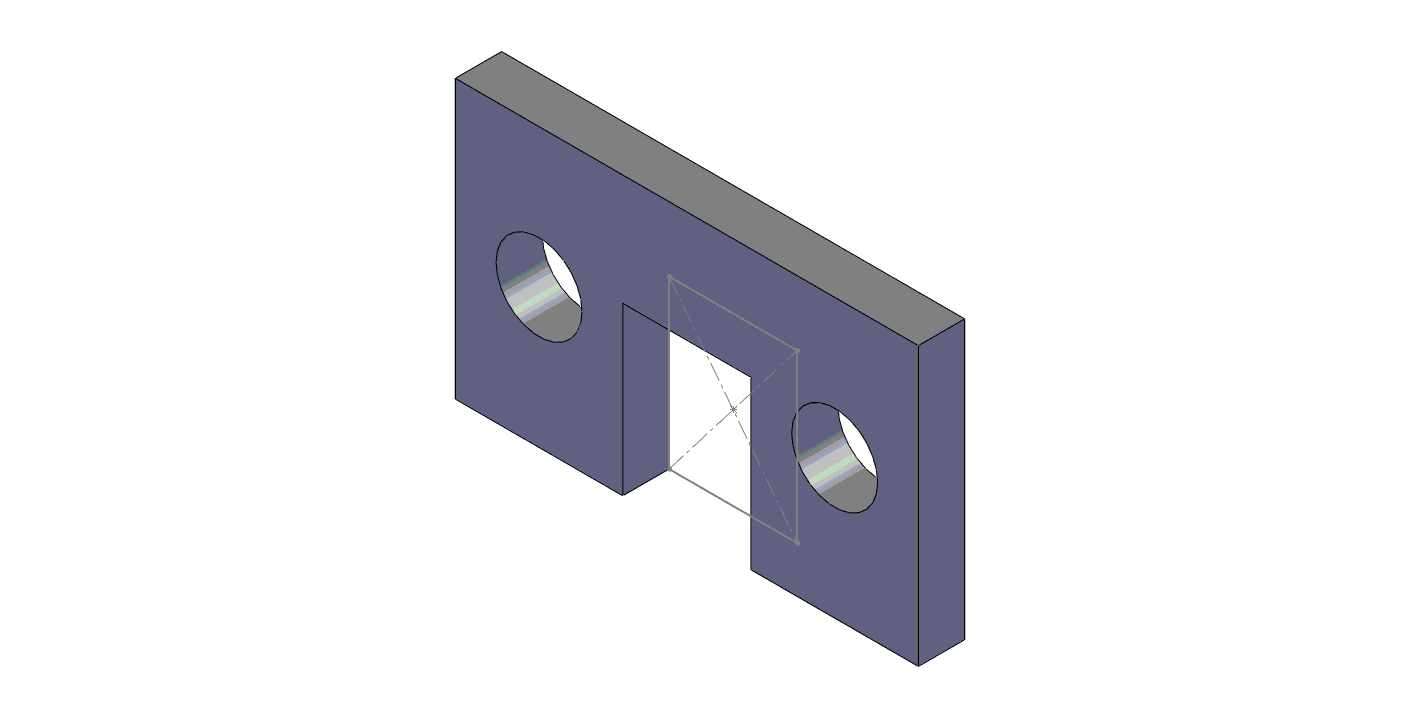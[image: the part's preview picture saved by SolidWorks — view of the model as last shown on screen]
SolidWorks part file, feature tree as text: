
SOLIDWORKS PART (.sldprt)
format: sldprt  version: not decoded by parser v0  size: 173,056 bytes
history: native  units: mm
features: sketch x4, material x1, extrude x1, hole x1 (+12 scaffold rows collapsed)
feature tree (19):
  scaffold x12  (default folders/planes/origin — collapsed)
  material  "Material <not specified>"
  sketch  "Sketch1"  dims[D1=4.3942mm D2=5.715mm]
  sketch  "Sketch2"  dims[D1=15.875mm D2=9.525mm]
  extrude  "Boss-Extrude1"  Depth=1.5875mm
  hole  "#4 Clearance Hole1"  Diameter=2.9464mm Depth=1.5875mm
  sketch  "Sketch5"
  sketch  "Sketch4"  dims[hole-wizard template sketch: 60 standard entries collapsed; hole parameters kept: c18.Thru Hole Depth=1.5875mm]
decode coverage: 5 of 6 modeling features carry decoded parameters
note: ~ marks probable driven/reference dimensions
note: suppression state not decoded; provenance and decode notes live in map.json
